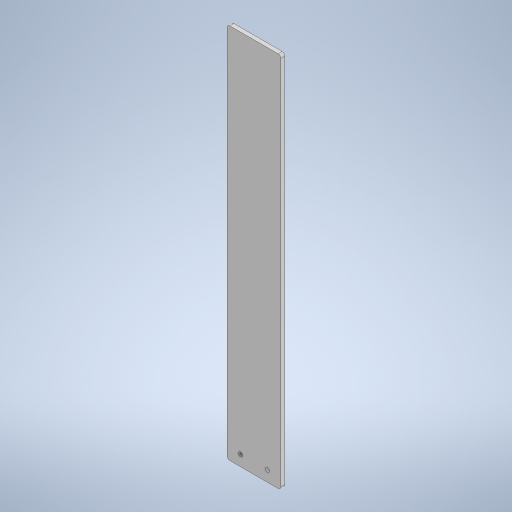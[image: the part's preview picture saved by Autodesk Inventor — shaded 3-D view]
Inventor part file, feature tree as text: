
AUTODESK INVENTOR PART (.ipt)
format: ipt  version: 2024.3 (Build 283343000, 343)  size: 249,344 bytes
history: native  units: mm
features: sketch x2, other x1, extrude x1, hole x1, fillet x1
ambient origin geometry x8: Origin, YZ Plane, XZ Plane, XY Plane, X Axis, Y Axis, Z Axis, Center Point
bodies: Body1 (feature_tree)
feature tree (6):
  other  "ソリッド1"
  extrude  "押し出し1"  Depth=40.0mm
  hole  "穴1"  [1 undecoded]
  fillet  "フィレット1"  Radius=3.0mm
  sketch  "スケッチ1"
  sketch  "スケッチ2"
note: 1 required parameter value undecoded (feature->parameter linkage not recoverable at this tier; creation-order binding heuristic only, values carry confidence <= 0.55)
